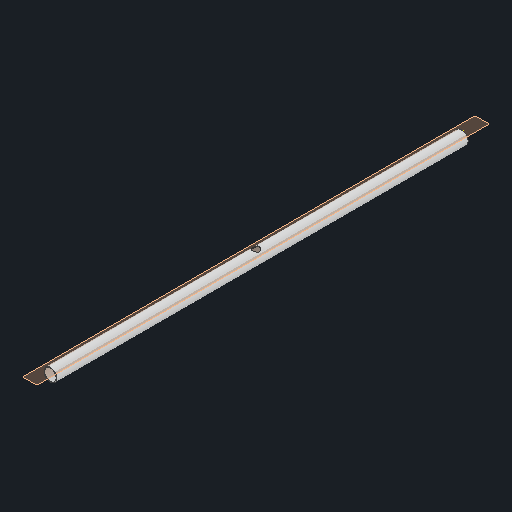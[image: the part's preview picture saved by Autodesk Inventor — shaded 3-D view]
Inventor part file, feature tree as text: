
AUTODESK INVENTOR PART (.ipt)
format: ipt  version: 2024 (Build 280153000, 153)  size: 187,392 bytes
history: native  units: mm
features: sketch x3, extrude x2, other x1, plane x1
ambient origin geometry x8: Origin, YZ Plane, XZ Plane, XY Plane, X Axis, Y Axis, Z Axis, Center Point
bodies: Body1 (feature_tree)
feature tree (7):
  other  "Sólido1"
  extrude  "Extrusión1"  Depth=170.62mm
  plane  "Plano de trabajo4"
  sketch  "Boceto5"  dims[d2=6000.0mm d3=0.0mm d17=69.75mm]
  extrude  "Extrusión5"  Depth=6000.0mm
  sketch  "Boceto1"  dims[d0=190.0mm d1=170.62mm]
  sketch  "Boceto6"  dims[d18=105.0mm d19=60.0mm d20=0.0mm d7=0.5mm d8=0.872665mm d9=0.5mm d10=0.872665mm]
